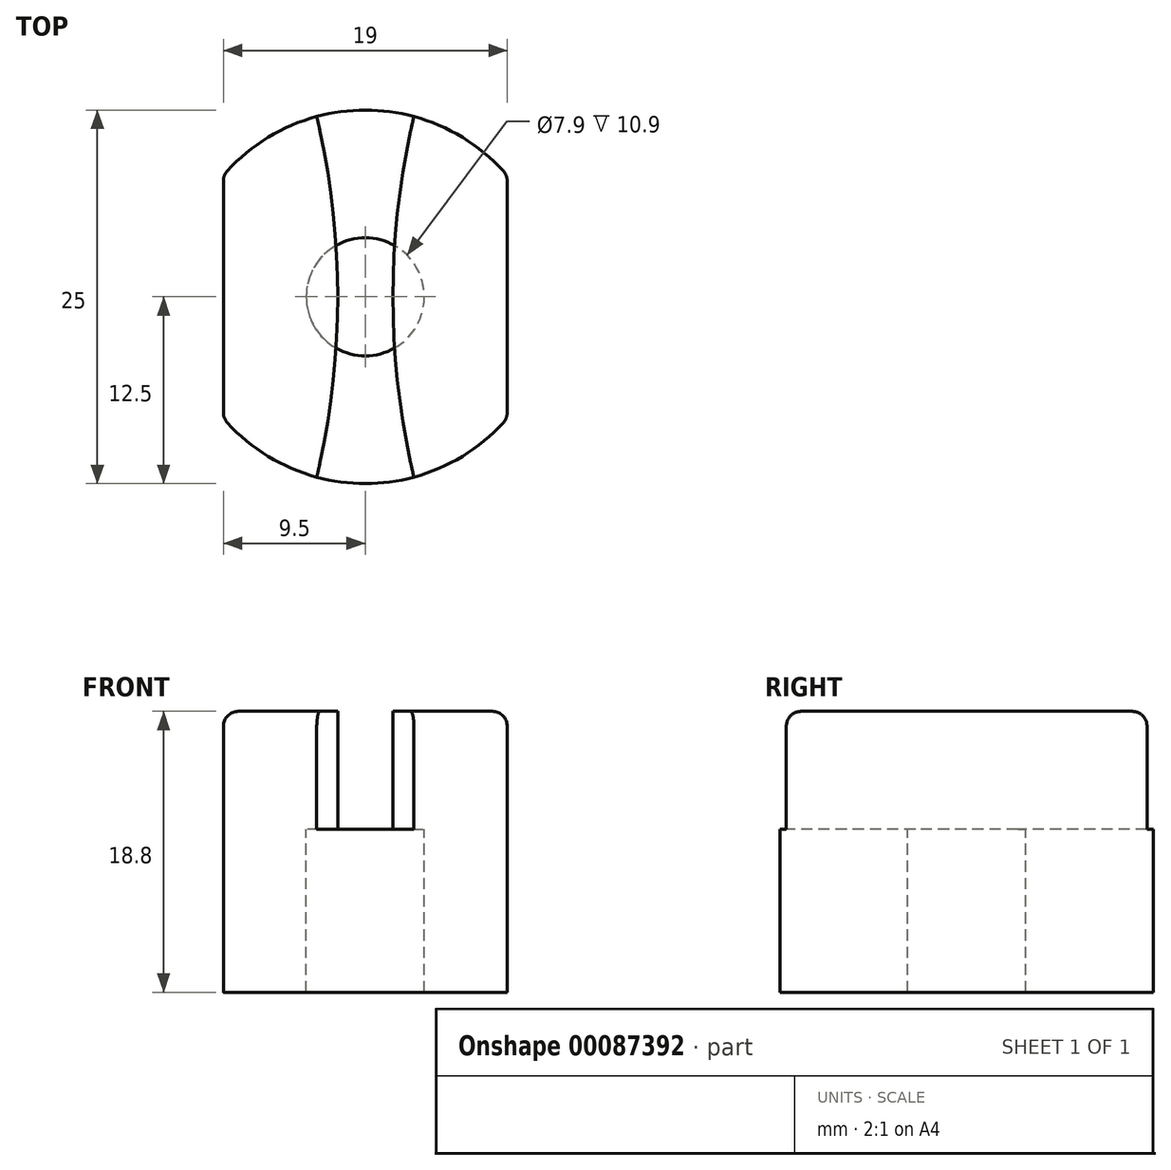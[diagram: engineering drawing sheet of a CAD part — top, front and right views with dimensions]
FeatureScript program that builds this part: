
annotation { "Feature Type Name" : "Feature", "Feature Type Description" : "" }
export const myFeature = defineFeature(function(context is Context, id is Id, definition is map)
    precondition{}
    {
        {
            var Q0;
            Q0=qCreatedBy(makeId("Top.planeOp"),FACE);
            var sketch = newSketch(context, id + "F0", { "sketchPlane" : qUnion([Q0])});
            skArc(sketch, "E0", {"start": v(9.5, 8.12) * mm, "mid": v(6.67, 10.57) * mm, "end": v(3.25, 12.07) * mm});
            skLineSegment(sketch, "E1", {"start": v(-9.5, 8.12) * mm, "end": v(-9.5, -8.12) * mm});
            skLineSegment(sketch, "E2.MirrorCS", {"start": v(9.5, 8.12) * mm, "end": v(9.5, -8.12) * mm});
            skArc(sketch, "E3.MirrorC", {"start": v(-3.25, 12.07) * mm, "mid": v(-1.85, 0) * mm, "end": v(-3.25, -12.07) * mm});
            skArc(sketch, "E4.MirrorC", {"start": v(3.25, 12.07) * mm, "mid": v(1.85, 0) * mm, "end": v(3.25, -12.07) * mm});
            skPoint(sketch, "E5.orphan", {"position": v(9.5, 25.8) * mm});
            skPoint(sketch, "E6.orphan", {"position": v(9.5, -22.99) * mm});
            skPoint(sketch, "E7.orphan", {"position": v(-9.5, -22.99) * mm});
            skPoint(sketch, "E8.orphan", {"position": v(-9.5, 25.8) * mm});
            skArc(sketch, "E9.trimOffspring", {"start": v(-9.5, -8.12) * mm, "mid": v(-6.67, -10.57) * mm, "end": v(-3.25, -12.07) * mm});
            skArc(sketch, "E10.trimOffspring", {"start": v(-3.25, 12.07) * mm, "mid": v(-6.67, 10.57) * mm, "end": v(-9.5, 8.12) * mm});
            skArc(sketch, "E11.trimOffspring", {"start": v(3.25, -12.07) * mm, "mid": v(6.67, -10.57) * mm, "end": v(9.5, -8.12) * mm});
            skSolve(sketch);
        }
        {
            var Q0;
            Q0 = qSketchRegion(id + "F0", true);
            extrude(context, id + "F1", {"entities" : qUnion([Q0]), "depth" : 7.9 * mm});
        }
        {
            var Q0;
            Q0=makeQuery(id+"F1.opExtrude","CAP_FACE",FACE,{"disambiguationData":[OSD([sQuery(id+"F0.wireOp",EDGE,"E0"),sQuery(id+"F0.wireOp",EDGE,"E2.MirrorCS"),sQuery(id+"F0.wireOp",EDGE,"E4.MirrorC"),sQuery(id+"F0.wireOp",EDGE,"E11.trimOffspring")])],"isStart":true});
            var sketch = newSketch(context, id + "F2", { "sketchPlane" : qUnion([Q0])});
            skArc(sketch, "E12", {"start": v(-9.5, -8.12) * mm, "mid": v(0, -12.5) * mm, "end": v(9.5, -8.12) * mm});
            skLineSegment(sketch, "E13", {"start": v(-9.5, -8.12) * mm, "end": v(-9.5, 8.12) * mm});
            skLineSegment(sketch, "E14.MirrorCS", {"start": v(9.5, -8.12) * mm, "end": v(9.5, 8.12) * mm});
            skArc(sketch, "E15.trimOffspring", {"start": v(9.5, 8.12) * mm, "mid": v(0, 12.5) * mm, "end": v(-9.5, 8.12) * mm});
            skPoint(sketch, "E16.orphan", {"position": v(9.5, -36.93) * mm});
            skPoint(sketch, "E17.orphan", {"position": v(-9.5, -36.93) * mm});
            skPoint(sketch, "E18.orphan", {"position": v(-9.5, 21.33) * mm});
            skPoint(sketch, "E19.orphan", {"position": v(9.5, 21.33) * mm});
            skCircle(sketch, "E20", {"center": v(0, 0) * mm, "radius": 3.95 * mm});
            skSolve(sketch);
        }
        {
            var Q0;
            Q0 = qSketchRegion(id + "F2", true);
            extrude(context, id + "F3", {"entities" : qUnion([Q0]), "operationType" : NewBodyOperationType.ADD, "depth" : 10.9 * mm});
        }
        {
            var Q0;
            Q0=makeQuery(id+"F1.opExtrude","SWEPT_EDGE",EDGE,{"disambiguationData":[OSD([sQuery(id+"F0.wireOp",EDGE,"E1"),sQuery(id+"F0.wireOp",EDGE,"E9.trimOffspring")])]});
            var Q1;
            Q1=makeQuery(id+"F1.opExtrude","SWEPT_EDGE",EDGE,{"disambiguationData":[OSD([sQuery(id+"F0.wireOp",EDGE,"E2.MirrorCS"),sQuery(id+"F0.wireOp",EDGE,"E11.trimOffspring")])]});
            var Q2;
            Q2=makeQuery(id+"F1.opExtrude","SWEPT_EDGE",EDGE,{"disambiguationData":[OSD([sQuery(id+"F0.wireOp",EDGE,"E0"),sQuery(id+"F0.wireOp",EDGE,"E2.MirrorCS")])]});
            var Q3;
            Q3=makeQuery(id+"F1.opExtrude","SWEPT_EDGE",EDGE,{"disambiguationData":[OSD([sQuery(id+"F0.wireOp",EDGE,"E1"),sQuery(id+"F0.wireOp",EDGE,"E10.trimOffspring")])]});
            fillet(context, id + "F4", {"entities" : qUnion([Q0, Q1, Q2, Q3]), "radius" : 1 * mm, "tangentPropagation" : true, "allowEdgeOverflow" : false});
        }
        {
            var Q0;
            Q0=makeQuery(id+"F1.opExtrude","CAP_EDGE",EDGE,{"disambiguationData":[OSD([sQuery(id+"F0.wireOp",EDGE,"E1")])],"isStart":false});
            var Q1;
            Q1=makeQuery(id+"F1.opExtrude","CAP_EDGE",EDGE,{"disambiguationData":[OSD([sQuery(id+"F0.wireOp",EDGE,"E11.trimOffspring")])],"isStart":false});
            fillet(context, id + "F5", {"entities" : qUnion([Q0, Q1]), "radius" : 1 * mm, "tangentPropagation" : true, "allowEdgeOverflow" : false});
        }
    });
